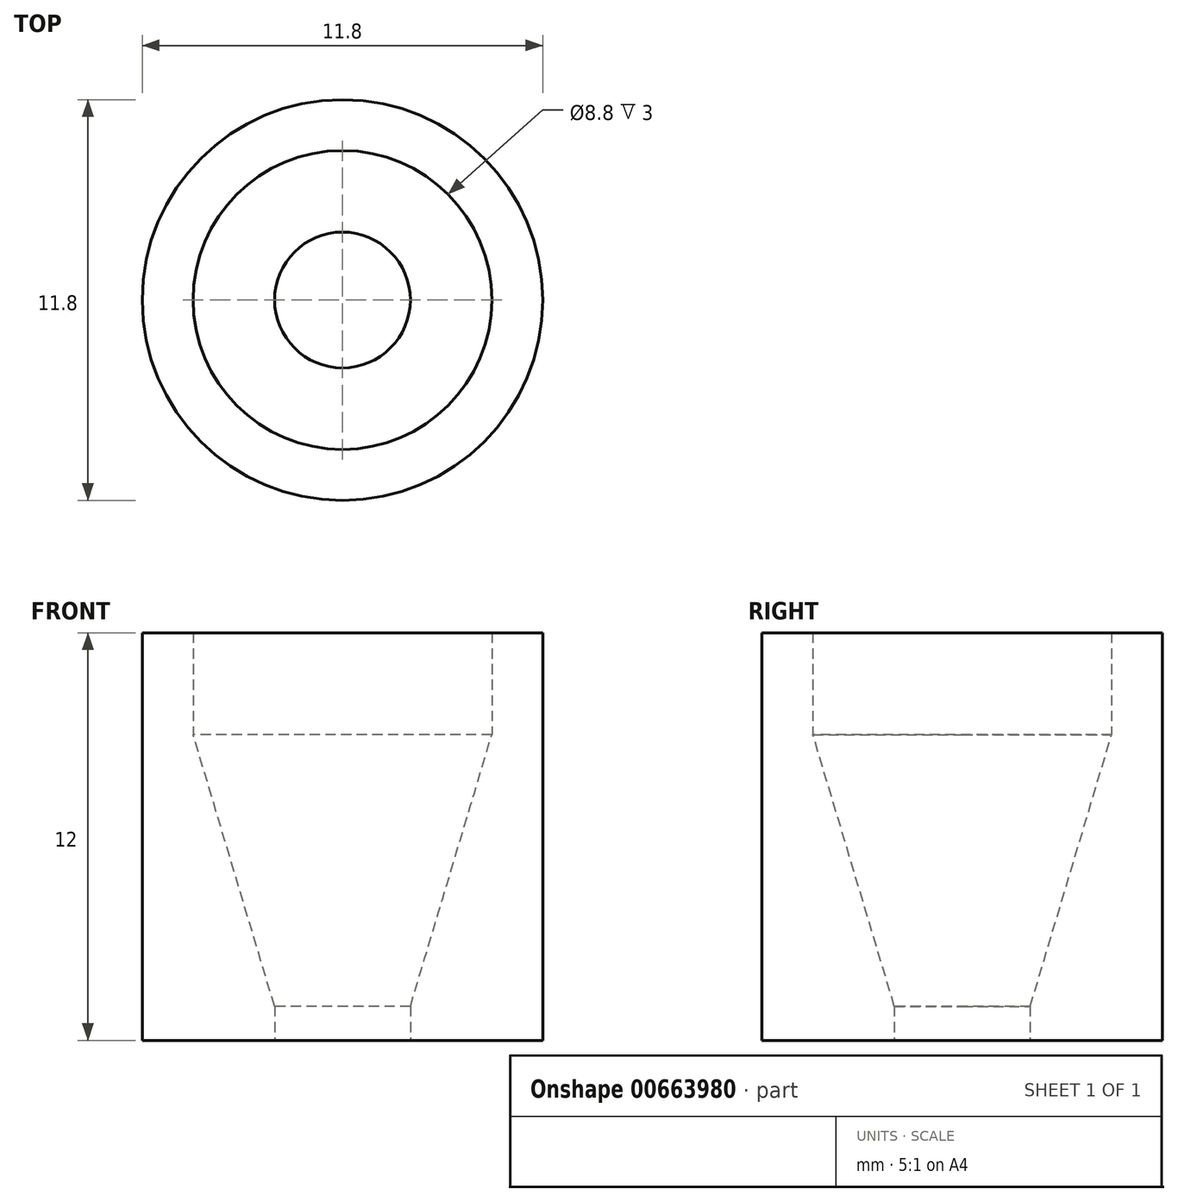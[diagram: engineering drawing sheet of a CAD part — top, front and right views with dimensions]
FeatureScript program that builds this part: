
annotation { "Feature Type Name" : "Feature", "Feature Type Description" : "" }
export const myFeature = defineFeature(function(context is Context, id is Id, definition is map)
    precondition{}
    {
        {
            var Q0;
            Q0=qCreatedBy(makeId("Top.planeOp"),FACE);
            var sketch = newSketch(context, id + "F0", { "sketchPlane" : qUnion([Q0])});
            skCircle(sketch, "E0", {"center": v(0, 0) * mm, "radius": 2 * mm});
            skCircle(sketch, "E1", {"center": v(0, 0) * mm, "radius": 5.9 * mm});
            skCircle(sketch, "E2", {"center": v(0, 0) * mm, "radius": 4.4 * mm, "construction": true});
            skSolve(sketch);
        }
        {
            var Q0;
            Q0=makeQuery(id+"F0.imprint","IMPRINT",FACE,{"disambiguationData":[TD([[makeQuery(id+"F0.imprint","IMPRINT",EDGE,{"derivedFrom":sQuery(id+"F0.wireOp",EDGE,"E0")}),-1.0]])]});
            extrude(context, id + "F1", {"entities" : qUnion([Q0]), "depth" : 9 * mm, "offsetDistance" : 25 * mm});
        }
        {
            var Q0;
            Q0=makeQuery(id+"F1.opExtrude","CAP_EDGE",EDGE,{"disambiguationData":[OSD([sQuery(id+"F0.wireOp",EDGE,"E0")])],"isStart":false});
            chamfer(context, id + "F2", {"entities" : qUnion([Q0]), "chamferType" : ChamferType.TWO_OFFSETS, "width1" : 8 * mm, "oppositeDirection" : false, "width2" : 2.4 * mm, "tangentPropagation" : true});
        }
        {
            var Q0;
            Q0=makeQuery(id+"F1.opExtrude","CAP_FACE",FACE,{"disambiguationData":[OSD([sQuery(id+"F0.wireOp",EDGE,"E0"),sQuery(id+"F0.wireOp",EDGE,"E1")])],"isStart":false});
            extrude(context, id + "F3", {"entities" : qUnion([Q0]), "operationType" : NewBodyOperationType.ADD, "depth" : 3 * mm, "offsetDistance" : 25 * mm});
        }
    });
